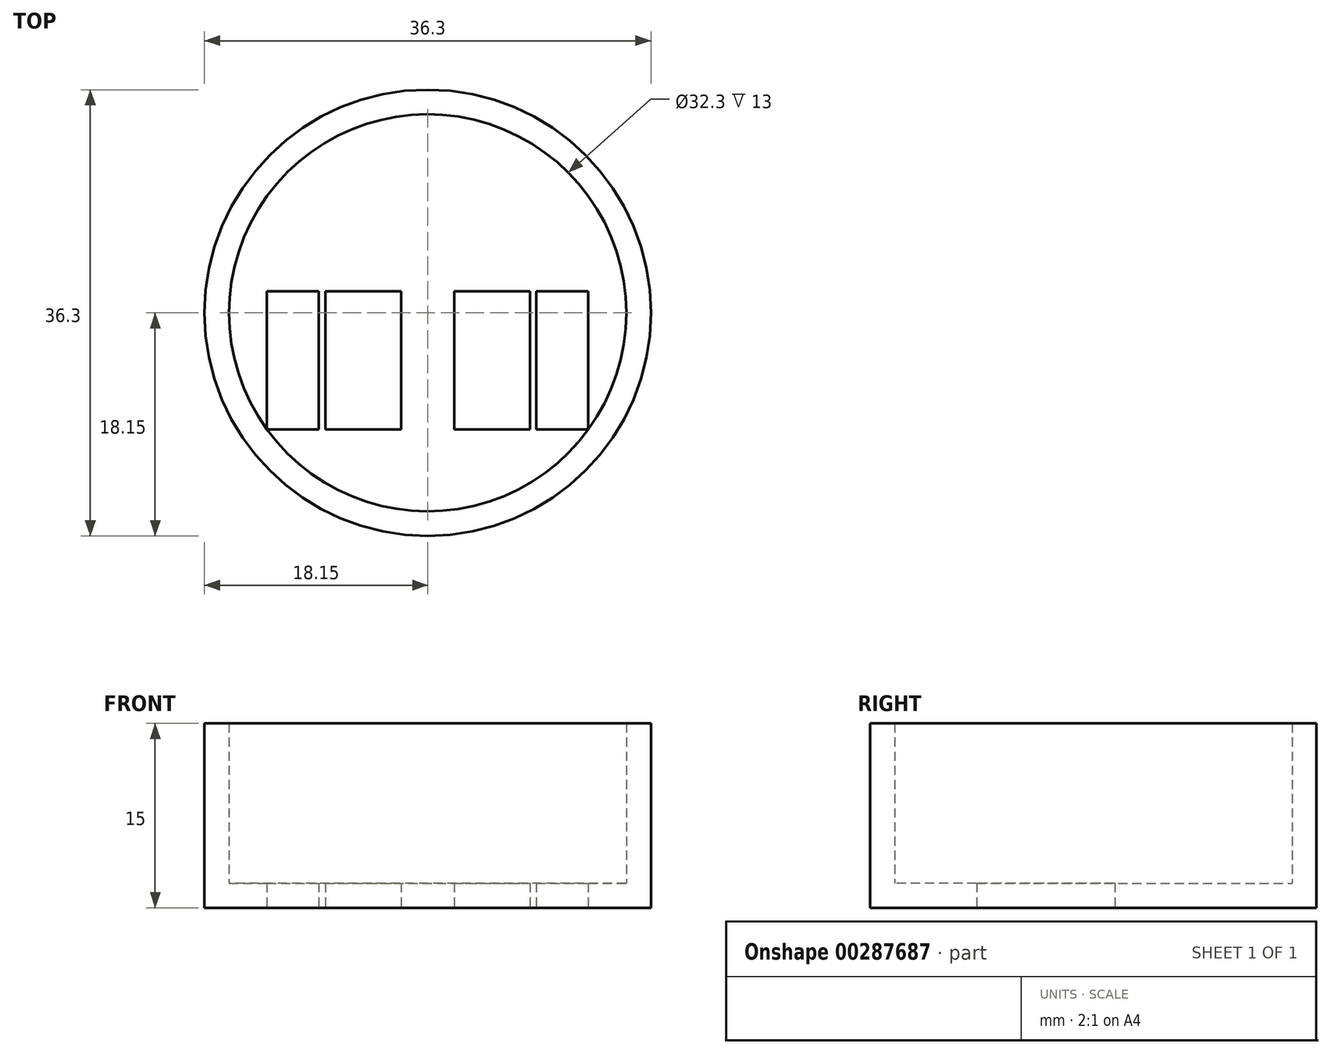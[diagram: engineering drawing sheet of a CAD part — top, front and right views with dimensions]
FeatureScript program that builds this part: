
annotation { "Feature Type Name" : "Feature", "Feature Type Description" : "" }
export const myFeature = defineFeature(function(context is Context, id is Id, definition is map)
    precondition{}
    {
        {
            var Q0;
            Q0=qCreatedBy(makeId("Top.planeOp"),FACE);
            var sketch = newSketch(context, id + "F0", { "sketchPlane" : qUnion([Q0])});
            skCircle(sketch, "E0", {"center": v(0, 0) * mm, "radius": 18.15 * mm});
            skLineSegment(sketch, "E1.bottom", {"start": v(-8.84, 15.85) * mm, "end": v(8.84, 15.85) * mm});
            skLineSegment(sketch, "E1.top", {"start": v(-8.84, -15.85) * mm, "end": v(8.84, -15.85) * mm});
            skLineSegment(sketch, "E1.left", {"start": v(-8.84, 15.85) * mm, "end": v(-8.84, -15.85) * mm});
            skLineSegment(sketch, "E1.right", {"start": v(8.84, 15.85) * mm, "end": v(8.84, -15.85) * mm});
            skLineSegment(sketch, "E2.bottom", {"start": v(-2.15, 18.02) * mm, "end": v(2.15, 18.02) * mm});
            skLineSegment(sketch, "E2.top", {"start": v(-2.15, -18.02) * mm, "end": v(2.15, -18.02) * mm});
            skLineSegment(sketch, "E2.left", {"start": v(-2.15, 18.02) * mm, "end": v(-2.15, -18.02) * mm});
            skLineSegment(sketch, "E2.right", {"start": v(2.15, 18.02) * mm, "end": v(2.15, -18.02) * mm});
            skLineSegment(sketch, "E3.bottom", {"start": v(-18.07, 1.75) * mm, "end": v(18.07, 1.75) * mm});
            skLineSegment(sketch, "E3.top", {"start": v(-18.07, -1.75) * mm, "end": v(18.07, -1.75) * mm});
            skLineSegment(sketch, "E3.left", {"start": v(-18.07, 1.75) * mm, "end": v(-18.07, -1.75) * mm});
            skLineSegment(sketch, "E3.right", {"start": v(18.07, 1.75) * mm, "end": v(18.07, -1.75) * mm});
            skLineSegment(sketch, "E4.bottom", {"start": v(-15.07, 1.75) * mm, "end": v(15.07, 1.75) * mm});
            skLineSegment(sketch, "E4.top", {"start": v(-15.07, -1.75) * mm, "end": v(15.07, -1.75) * mm});
            skLineSegment(sketch, "E4.left", {"start": v(-15.07, 1.75) * mm, "end": v(-15.07, -1.75) * mm});
            skLineSegment(sketch, "E4.right", {"start": v(15.07, 1.75) * mm, "end": v(15.07, -1.75) * mm});
            skCircle(sketch, "E5", {"center": v(0, 0) * mm, "radius": 16.15 * mm});
            skLineSegment(sketch, "E6.bottom", {"start": v(8.3, 13.85) * mm, "end": v(-8.3, 13.85) * mm});
            skLineSegment(sketch, "E6.top", {"start": v(8.3, -13.85) * mm, "end": v(-8.3, -13.85) * mm});
            skLineSegment(sketch, "E6.left", {"start": v(8.3, 13.85) * mm, "end": v(8.3, -13.85) * mm});
            skLineSegment(sketch, "E6.right", {"start": v(-8.3, 13.85) * mm, "end": v(-8.3, -13.85) * mm});
            skLineSegment(sketch, "E7.bottom", {"start": v(-13.07, 9.5) * mm, "end": v(13.07, 9.5) * mm});
            skLineSegment(sketch, "E7.top", {"start": v(-13.07, -9.5) * mm, "end": v(13.07, -9.5) * mm});
            skLineSegment(sketch, "E7.left", {"start": v(-13.07, 9.5) * mm, "end": v(-13.07, -9.5) * mm});
            skLineSegment(sketch, "E7.right", {"start": v(13.07, 9.5) * mm, "end": v(13.07, -9.5) * mm});
            skSolve(sketch);
        }
        {
            var Q0;
            Q0 = qSketchRegion(id + "F0", true);
            extrude(context, id + "F1", {"entities" : qUnion([Q0]), "depth" : 15 * mm});
        }
        {
            var Q0;
            {var subQ0=sQuery(id+"F0.wireOp",EDGE,"E2.bottom");Q0=makeQuery(id+"F0.imprint","IMPRINT",FACE,{"disambiguationData":[TD([[makeQuery(id+"F0.imprint","IMPRINT",EDGE,{"derivedFrom":subQ0}),1.0]])]});}
            var Q1;
            {var subQ0=sQuery(id+"F0.wireOp",EDGE,"E3.left");Q1=makeQuery(id+"F0.imprint","IMPRINT",FACE,{"disambiguationData":[TD([[makeQuery(id+"F0.imprint","IMPRINT",EDGE,{"derivedFrom":subQ0}),-1.0]])]});}
            var Q2;
            {var subQ0=sQuery(id+"F0.wireOp",EDGE,"E2.top");Q2=makeQuery(id+"F0.imprint","IMPRINT",FACE,{"disambiguationData":[TD([[makeQuery(id+"F0.imprint","IMPRINT",EDGE,{"derivedFrom":subQ0}),-1.0]])]});}
            var Q3;
            {var subQ0=sQuery(id+"F0.wireOp",EDGE,"E3.right");Q3=makeQuery(id+"F0.imprint","IMPRINT",FACE,{"disambiguationData":[TD([[makeQuery(id+"F0.imprint","IMPRINT",EDGE,{"derivedFrom":subQ0}),1.0]])]});}
            var Q4;
            {var subQ0=sQuery(id+"F0.wireOp",EDGE,"E1.bottom");var subQ5=sQuery(id+"F0.wireOp",EDGE,"E5");var subQ6=makeQuery(id+"F0.imprint","INTERSECT",VERTEX,{"disambiguationData":[OD(1.0)],"derivedFrom":[subQ0,subQ5]});Q4=makeQuery(id+"F0.imprint","IMPRINT",FACE,{"disambiguationData":[TD([[makeQuery(id+"F0.imprint","IMPRINT",EDGE,{"disambiguationData":[TD([[subQ6,-1.0]])],"derivedFrom":subQ5}),-1.0]])]});}
            var Q5;
            {var subQ0=sQuery(id+"F0.wireOp",EDGE,"E1.bottom");var subQ5=sQuery(id+"F0.wireOp",EDGE,"E5");var subQ7=makeQuery(id+"F0.imprint","INTERSECT",VERTEX,{"disambiguationData":[OD(0.0)],"derivedFrom":[subQ0,subQ5]});Q5=makeQuery(id+"F0.imprint","IMPRINT",FACE,{"disambiguationData":[TD([[makeQuery(id+"F0.imprint","IMPRINT",EDGE,{"disambiguationData":[TD([[subQ7,1.0]])],"derivedFrom":subQ5}),-1.0]])]});}
            var Q6;
            {var subQ0=sQuery(id+"F0.wireOp",EDGE,"E1.top");var subQ5=sQuery(id+"F0.wireOp",EDGE,"E5");var subQ6=makeQuery(id+"F0.imprint","INTERSECT",VERTEX,{"disambiguationData":[OD(0.0)],"derivedFrom":[subQ0,subQ5]});Q6=makeQuery(id+"F0.imprint","IMPRINT",FACE,{"disambiguationData":[TD([[makeQuery(id+"F0.imprint","IMPRINT",EDGE,{"disambiguationData":[TD([[subQ6,-1.0]])],"derivedFrom":subQ5}),-1.0]])]});}
            var Q7;
            {var subQ0=sQuery(id+"F0.wireOp",EDGE,"E1.top");var subQ5=sQuery(id+"F0.wireOp",EDGE,"E5");var subQ7=makeQuery(id+"F0.imprint","INTERSECT",VERTEX,{"disambiguationData":[OD(1.0)],"derivedFrom":[subQ0,subQ5]});Q7=makeQuery(id+"F0.imprint","IMPRINT",FACE,{"disambiguationData":[TD([[makeQuery(id+"F0.imprint","IMPRINT",EDGE,{"disambiguationData":[TD([[subQ7,1.0]])],"derivedFrom":subQ5}),-1.0]])]});}
            var Q8;
            {var subQ3=sQuery(id+"F0.wireOp",EDGE,"E5");var subQ5=sQuery(id+"F0.wireOp",EDGE,"E1.right");var subQ7=makeQuery(id+"F0.imprint","INTERSECT",VERTEX,{"disambiguationData":[OD(0.0)],"derivedFrom":[subQ5,subQ3]});Q8=makeQuery(id+"F0.imprint","IMPRINT",FACE,{"disambiguationData":[TD([[makeQuery(id+"F0.imprint","IMPRINT",EDGE,{"disambiguationData":[TD([[subQ7,1.0]])],"derivedFrom":subQ5}),1.0]])]});}
            var Q9;
            {var subQ3=sQuery(id+"F0.wireOp",EDGE,"E5");var subQ5=sQuery(id+"F0.wireOp",EDGE,"E1.left");var subQ7=makeQuery(id+"F0.imprint","INTERSECT",VERTEX,{"disambiguationData":[OD(0.0)],"derivedFrom":[subQ5,subQ3]});Q9=makeQuery(id+"F0.imprint","IMPRINT",FACE,{"disambiguationData":[TD([[makeQuery(id+"F0.imprint","IMPRINT",EDGE,{"disambiguationData":[TD([[subQ7,1.0]])],"derivedFrom":subQ5}),-1.0]])]});}
            var Q10;
            {var subQ0=sQuery(id+"F0.wireOp",EDGE,"E5");var subQ6=sQuery(id+"F0.wireOp",EDGE,"E1.left");var subQ8=makeQuery(id+"F0.imprint","INTERSECT",VERTEX,{"disambiguationData":[OD(1.0)],"derivedFrom":[subQ6,subQ0]});Q10=makeQuery(id+"F0.imprint","IMPRINT",FACE,{"disambiguationData":[TD([[makeQuery(id+"F0.imprint","IMPRINT",EDGE,{"disambiguationData":[TD([[subQ8,-1.0]])],"derivedFrom":subQ6}),-1.0]])]});}
            var Q11;
            {var subQ0=sQuery(id+"F0.wireOp",EDGE,"E5");var subQ2=sQuery(id+"F0.wireOp",EDGE,"E1.right");var subQ3=makeQuery(id+"F0.imprint","INTERSECT",VERTEX,{"disambiguationData":[OD(1.0)],"derivedFrom":[subQ2,subQ0]});Q11=makeQuery(id+"F0.imprint","IMPRINT",FACE,{"disambiguationData":[TD([[makeQuery(id+"F0.imprint","IMPRINT",EDGE,{"disambiguationData":[TD([[subQ3,-1.0]])],"derivedFrom":subQ2}),1.0]])]});}
            var Q12;
            {var subQ1=sQuery(id+"F0.wireOp",EDGE,"E1.bottom");var subQ3=sQuery(id+"F0.wireOp",EDGE,"E5");var subQ4=makeQuery(id+"F0.imprint","INTERSECT",VERTEX,{"disambiguationData":[OD(0.0)],"derivedFrom":[subQ1,subQ3]});Q12=makeQuery(id+"F0.imprint","IMPRINT",FACE,{"disambiguationData":[TD([[makeQuery(id+"F0.imprint","IMPRINT",EDGE,{"disambiguationData":[TD([[subQ4,1.0]])],"derivedFrom":subQ1}),-1.0]])]});}
            var Q13;
            {var subQ1=sQuery(id+"F0.wireOp",EDGE,"E1.bottom");var subQ3=sQuery(id+"F0.wireOp",EDGE,"E5");var subQ4=makeQuery(id+"F0.imprint","INTERSECT",VERTEX,{"disambiguationData":[OD(1.0)],"derivedFrom":[subQ1,subQ3]});Q13=makeQuery(id+"F0.imprint","IMPRINT",FACE,{"disambiguationData":[TD([[makeQuery(id+"F0.imprint","IMPRINT",EDGE,{"disambiguationData":[TD([[subQ4,-1.0]])],"derivedFrom":subQ1}),-1.0]])]});}
            var Q14;
            {var subQ1=sQuery(id+"F0.wireOp",EDGE,"E1.top");var subQ3=sQuery(id+"F0.wireOp",EDGE,"E5");var subQ4=makeQuery(id+"F0.imprint","INTERSECT",VERTEX,{"disambiguationData":[OD(0.0)],"derivedFrom":[subQ1,subQ3]});Q14=makeQuery(id+"F0.imprint","IMPRINT",FACE,{"disambiguationData":[TD([[makeQuery(id+"F0.imprint","IMPRINT",EDGE,{"disambiguationData":[TD([[subQ4,1.0]])],"derivedFrom":subQ1}),1.0]])]});}
            var Q15;
            {var subQ1=sQuery(id+"F0.wireOp",EDGE,"E1.top");var subQ3=sQuery(id+"F0.wireOp",EDGE,"E5");var subQ4=makeQuery(id+"F0.imprint","INTERSECT",VERTEX,{"disambiguationData":[OD(1.0)],"derivedFrom":[subQ1,subQ3]});Q15=makeQuery(id+"F0.imprint","IMPRINT",FACE,{"disambiguationData":[TD([[makeQuery(id+"F0.imprint","IMPRINT",EDGE,{"disambiguationData":[TD([[subQ4,-1.0]])],"derivedFrom":subQ1}),1.0]])]});}
            var Q16;
            {var subQ0=sQuery(id+"F0.wireOp",EDGE,"E2.bottom");Q16=makeQuery(id+"F0.imprint","IMPRINT",FACE,{"disambiguationData":[TD([[makeQuery(id+"F0.imprint","IMPRINT",EDGE,{"derivedFrom":subQ0}),-1.0]])]});}
            var Q17;
            {var subQ0=sQuery(id+"F0.wireOp",EDGE,"E2.top");Q17=makeQuery(id+"F0.imprint","IMPRINT",FACE,{"disambiguationData":[TD([[makeQuery(id+"F0.imprint","IMPRINT",EDGE,{"derivedFrom":subQ0}),1.0]])]});}
            var Q18;
            {var subQ0=sQuery(id+"F0.wireOp",EDGE,"E3.left");Q18=makeQuery(id+"F0.imprint","IMPRINT",FACE,{"disambiguationData":[TD([[makeQuery(id+"F0.imprint","IMPRINT",EDGE,{"derivedFrom":subQ0}),1.0]])]});}
            var Q19;
            {var subQ0=sQuery(id+"F0.wireOp",EDGE,"E3.right");Q19=makeQuery(id+"F0.imprint","IMPRINT",FACE,{"disambiguationData":[TD([[makeQuery(id+"F0.imprint","IMPRINT",EDGE,{"derivedFrom":subQ0}),-1.0]])]});}
            var Q20;
            {var subQ0=sQuery(id+"F0.wireOp",EDGE,"E6.bottom");var subQ1=sQuery(id+"F0.wireOp",EDGE,"E2.left");var subQ2=makeQuery(id+"F0.imprint","INTERSECT",VERTEX,{"derivedFrom":[subQ1,subQ0]});Q20=makeQuery(id+"F0.imprint","IMPRINT",FACE,{"disambiguationData":[TD([[makeQuery(id+"F0.imprint","IMPRINT",EDGE,{"disambiguationData":[TD([[subQ2,-1.0]])],"derivedFrom":subQ1}),1.0]])]});}
            var Q21;
            {var subQ0=sQuery(id+"F0.wireOp",EDGE,"E4.bottom");var subQ1=sQuery(id+"F0.wireOp",EDGE,"E1.right");var subQ2=makeQuery(id+"F0.imprint","INTERSECT",VERTEX,{"derivedFrom":[subQ1,subQ0]});Q21=makeQuery(id+"F0.imprint","IMPRINT",FACE,{"disambiguationData":[TD([[makeQuery(id+"F0.imprint","IMPRINT",EDGE,{"disambiguationData":[TD([[subQ2,-1.0]])],"derivedFrom":subQ1}),1.0]])]});}
            var Q22;
            {var subQ0=sQuery(id+"F0.wireOp",EDGE,"E7.bottom");var subQ1=sQuery(id+"F0.wireOp",EDGE,"E1.left");var subQ2=makeQuery(id+"F0.imprint","INTERSECT",VERTEX,{"derivedFrom":[subQ1,subQ0]});Q22=makeQuery(id+"F0.imprint","IMPRINT",FACE,{"disambiguationData":[TD([[makeQuery(id+"F0.imprint","IMPRINT",EDGE,{"disambiguationData":[TD([[subQ2,-1.0]])],"derivedFrom":subQ1}),-1.0]])]});}
            var Q23;
            {var subQ0=sQuery(id+"F0.wireOp",EDGE,"E2.right");var subQ1=sQuery(id+"F0.wireOp",EDGE,"E1.top");var subQ2=makeQuery(id+"F0.imprint","INTERSECT",VERTEX,{"derivedFrom":[subQ1,subQ0]});Q23=makeQuery(id+"F0.imprint","IMPRINT",FACE,{"disambiguationData":[TD([[makeQuery(id+"F0.imprint","IMPRINT",EDGE,{"disambiguationData":[TD([[subQ2,-1.0]])],"derivedFrom":subQ1}),1.0]])]});}
            var Q24;
            {var subQ0=sQuery(id+"F0.wireOp",EDGE,"E4.top");var subQ1=sQuery(id+"F0.wireOp",EDGE,"E1.left");var subQ2=makeQuery(id+"F0.imprint","INTERSECT",VERTEX,{"derivedFrom":[subQ1,subQ0]});Q24=makeQuery(id+"F0.imprint","IMPRINT",FACE,{"disambiguationData":[TD([[makeQuery(id+"F0.imprint","IMPRINT",EDGE,{"disambiguationData":[TD([[subQ2,-1.0]])],"derivedFrom":subQ1}),-1.0]])]});}
            var Q25;
            {var subQ0=sQuery(id+"F0.wireOp",EDGE,"E5");var subQ1=sQuery(id+"F0.wireOp",EDGE,"E1.right");var subQ2=makeQuery(id+"F0.imprint","INTERSECT",VERTEX,{"disambiguationData":[OD(0.0)],"derivedFrom":[subQ1,subQ0]});Q25=makeQuery(id+"F0.imprint","IMPRINT",FACE,{"disambiguationData":[TD([[makeQuery(id+"F0.imprint","IMPRINT",EDGE,{"disambiguationData":[TD([[subQ2,-1.0]])],"derivedFrom":subQ1}),1.0]])]});}
            var Q26;
            {var subQ0=sQuery(id+"F0.wireOp",EDGE,"E7.top");var subQ1=sQuery(id+"F0.wireOp",EDGE,"E1.left");var subQ2=makeQuery(id+"F0.imprint","INTERSECT",VERTEX,{"derivedFrom":[subQ1,subQ0]});Q26=makeQuery(id+"F0.imprint","IMPRINT",FACE,{"disambiguationData":[TD([[makeQuery(id+"F0.imprint","IMPRINT",EDGE,{"disambiguationData":[TD([[subQ2,-1.0]])],"derivedFrom":subQ1}),-1.0]])]});}
            var Q27;
            {var subQ0=sQuery(id+"F0.wireOp",EDGE,"E7.top");var subQ1=sQuery(id+"F0.wireOp",EDGE,"E1.right");var subQ2=makeQuery(id+"F0.imprint","INTERSECT",VERTEX,{"derivedFrom":[subQ1,subQ0]});Q27=makeQuery(id+"F0.imprint","IMPRINT",FACE,{"disambiguationData":[TD([[makeQuery(id+"F0.imprint","IMPRINT",EDGE,{"disambiguationData":[TD([[subQ2,-1.0]])],"derivedFrom":subQ1}),1.0]])]});}
            var Q28;
            {var subQ0=sQuery(id+"F0.wireOp",EDGE,"E7.bottom");var subQ1=sQuery(id+"F0.wireOp",EDGE,"E1.right");var subQ2=makeQuery(id+"F0.imprint","INTERSECT",VERTEX,{"derivedFrom":[subQ1,subQ0]});Q28=makeQuery(id+"F0.imprint","IMPRINT",FACE,{"disambiguationData":[TD([[makeQuery(id+"F0.imprint","IMPRINT",EDGE,{"disambiguationData":[TD([[subQ2,-1.0]])],"derivedFrom":subQ1}),1.0]])]});}
            var Q29;
            {var subQ1=sQuery(id+"F0.wireOp",EDGE,"E3.bottom");var subQ3=sQuery(id+"F0.wireOp",EDGE,"E5");var subQ4=makeQuery(id+"F0.imprint","INTERSECT",VERTEX,{"disambiguationData":[OD(0.0)],"derivedFrom":[subQ1,subQ3]});Q29=makeQuery(id+"F0.imprint","IMPRINT",FACE,{"disambiguationData":[TD([[makeQuery(id+"F0.imprint","IMPRINT",EDGE,{"disambiguationData":[TD([[subQ4,-1.0]])],"derivedFrom":subQ1}),1.0]])]});}
            var Q30;
            {var subQ1=sQuery(id+"F0.wireOp",EDGE,"E3.top");var subQ3=sQuery(id+"F0.wireOp",EDGE,"E5");var subQ4=makeQuery(id+"F0.imprint","INTERSECT",VERTEX,{"disambiguationData":[OD(1.0)],"derivedFrom":[subQ1,subQ3]});Q30=makeQuery(id+"F0.imprint","IMPRINT",FACE,{"disambiguationData":[TD([[makeQuery(id+"F0.imprint","IMPRINT",EDGE,{"disambiguationData":[TD([[subQ4,1.0]])],"derivedFrom":subQ1}),-1.0]])]});}
            var Q31;
            {var subQ0=sQuery(id+"F0.wireOp",EDGE,"E4.top");var subQ1=sQuery(id+"F0.wireOp",EDGE,"E2.left");var subQ2=makeQuery(id+"F0.imprint","INTERSECT",VERTEX,{"derivedFrom":[subQ1,subQ0]});Q31=makeQuery(id+"F0.imprint","IMPRINT",FACE,{"disambiguationData":[TD([[makeQuery(id+"F0.imprint","IMPRINT",EDGE,{"disambiguationData":[TD([[subQ2,-1.0]])],"derivedFrom":subQ1}),1.0]])]});}
            var Q32;
            {var subQ0=sQuery(id+"F0.wireOp",EDGE,"E6.bottom");var subQ1=sQuery(id+"F0.wireOp",EDGE,"E2.right");var subQ2=makeQuery(id+"F0.imprint","INTERSECT",VERTEX,{"derivedFrom":[subQ1,subQ0]});Q32=makeQuery(id+"F0.imprint","IMPRINT",FACE,{"disambiguationData":[TD([[makeQuery(id+"F0.imprint","IMPRINT",EDGE,{"disambiguationData":[TD([[subQ2,-1.0]])],"derivedFrom":subQ1}),1.0]])]});}
            var Q33;
            {var subQ0=sQuery(id+"F0.wireOp",EDGE,"E7.bottom");var subQ1=sQuery(id+"F0.wireOp",EDGE,"E2.left");var subQ2=makeQuery(id+"F0.imprint","INTERSECT",VERTEX,{"derivedFrom":[subQ1,subQ0]});Q33=makeQuery(id+"F0.imprint","IMPRINT",FACE,{"disambiguationData":[TD([[makeQuery(id+"F0.imprint","IMPRINT",EDGE,{"disambiguationData":[TD([[subQ2,-1.0]])],"derivedFrom":subQ1}),-1.0]])]});}
            var Q34;
            {var subQ0=sQuery(id+"F0.wireOp",EDGE,"E4.top");var subQ1=sQuery(id+"F0.wireOp",EDGE,"E1.right");var subQ2=makeQuery(id+"F0.imprint","INTERSECT",VERTEX,{"derivedFrom":[subQ1,subQ0]});Q34=makeQuery(id+"F0.imprint","IMPRINT",FACE,{"disambiguationData":[TD([[makeQuery(id+"F0.imprint","IMPRINT",EDGE,{"disambiguationData":[TD([[subQ2,-1.0]])],"derivedFrom":subQ1}),1.0]])]});}
            var Q35;
            {var subQ0=sQuery(id+"F0.wireOp",EDGE,"E4.bottom");var subQ1=sQuery(id+"F0.wireOp",EDGE,"E2.right");var subQ2=makeQuery(id+"F0.imprint","INTERSECT",VERTEX,{"derivedFrom":[subQ1,subQ0]});Q35=makeQuery(id+"F0.imprint","IMPRINT",FACE,{"disambiguationData":[TD([[makeQuery(id+"F0.imprint","IMPRINT",EDGE,{"disambiguationData":[TD([[subQ2,-1.0]])],"derivedFrom":subQ1}),1.0]])]});}
            var Q36;
            {var subQ1=sQuery(id+"F0.wireOp",EDGE,"E3.bottom");var subQ3=sQuery(id+"F0.wireOp",EDGE,"E5");var subQ4=makeQuery(id+"F0.imprint","INTERSECT",VERTEX,{"disambiguationData":[OD(1.0)],"derivedFrom":[subQ1,subQ3]});Q36=makeQuery(id+"F0.imprint","IMPRINT",FACE,{"disambiguationData":[TD([[makeQuery(id+"F0.imprint","IMPRINT",EDGE,{"disambiguationData":[TD([[subQ4,1.0]])],"derivedFrom":subQ1}),1.0]])]});}
            var Q37;
            {var subQ0=sQuery(id+"F0.wireOp",EDGE,"E5");var subQ1=sQuery(id+"F0.wireOp",EDGE,"E1.bottom");var subQ2=makeQuery(id+"F0.imprint","INTERSECT",VERTEX,{"disambiguationData":[OD(0.0)],"derivedFrom":[subQ1,subQ0]});Q37=makeQuery(id+"F0.imprint","IMPRINT",FACE,{"disambiguationData":[TD([[makeQuery(id+"F0.imprint","IMPRINT",EDGE,{"disambiguationData":[TD([[subQ2,-1.0]])],"derivedFrom":subQ1}),-1.0]])]});}
            var Q38;
            {var subQ1=sQuery(id+"F0.wireOp",EDGE,"E3.top");var subQ3=sQuery(id+"F0.wireOp",EDGE,"E5");var subQ4=makeQuery(id+"F0.imprint","INTERSECT",VERTEX,{"disambiguationData":[OD(0.0)],"derivedFrom":[subQ1,subQ3]});Q38=makeQuery(id+"F0.imprint","IMPRINT",FACE,{"disambiguationData":[TD([[makeQuery(id+"F0.imprint","IMPRINT",EDGE,{"disambiguationData":[TD([[subQ4,-1.0]])],"derivedFrom":subQ1}),-1.0]])]});}
            var Q39;
            {var subQ0=sQuery(id+"F0.wireOp",EDGE,"E2.left");var subQ1=sQuery(id+"F0.wireOp",EDGE,"E1.bottom");var subQ2=makeQuery(id+"F0.imprint","INTERSECT",VERTEX,{"derivedFrom":[subQ1,subQ0]});Q39=makeQuery(id+"F0.imprint","IMPRINT",FACE,{"disambiguationData":[TD([[makeQuery(id+"F0.imprint","IMPRINT",EDGE,{"disambiguationData":[TD([[subQ2,-1.0]])],"derivedFrom":subQ1}),-1.0]])]});}
            var Q40;
            {var subQ0=sQuery(id+"F0.wireOp",EDGE,"E4.bottom");var subQ1=sQuery(id+"F0.wireOp",EDGE,"E2.left");var subQ2=makeQuery(id+"F0.imprint","INTERSECT",VERTEX,{"derivedFrom":[subQ1,subQ0]});Q40=makeQuery(id+"F0.imprint","IMPRINT",FACE,{"disambiguationData":[TD([[makeQuery(id+"F0.imprint","IMPRINT",EDGE,{"disambiguationData":[TD([[subQ2,-1.0]])],"derivedFrom":subQ1}),-1.0]])]});}
            var Q41;
            {var subQ0=sQuery(id+"F0.wireOp",EDGE,"E7.top");var subQ1=sQuery(id+"F0.wireOp",EDGE,"E2.left");var subQ2=makeQuery(id+"F0.imprint","INTERSECT",VERTEX,{"derivedFrom":[subQ1,subQ0]});Q41=makeQuery(id+"F0.imprint","IMPRINT",FACE,{"disambiguationData":[TD([[makeQuery(id+"F0.imprint","IMPRINT",EDGE,{"disambiguationData":[TD([[subQ2,-1.0]])],"derivedFrom":subQ1}),-1.0]])]});}
            var Q42;
            {var subQ0=sQuery(id+"F0.wireOp",EDGE,"E5");var subQ1=sQuery(id+"F0.wireOp",EDGE,"E1.left");var subQ2=makeQuery(id+"F0.imprint","INTERSECT",VERTEX,{"disambiguationData":[OD(0.0)],"derivedFrom":[subQ1,subQ0]});Q42=makeQuery(id+"F0.imprint","IMPRINT",FACE,{"disambiguationData":[TD([[makeQuery(id+"F0.imprint","IMPRINT",EDGE,{"disambiguationData":[TD([[subQ2,-1.0]])],"derivedFrom":subQ1}),-1.0]])]});}
            var Q43;
            {var subQ0=sQuery(id+"F0.wireOp",EDGE,"E7.top");var subQ1=sQuery(id+"F0.wireOp",EDGE,"E2.right");var subQ2=makeQuery(id+"F0.imprint","INTERSECT",VERTEX,{"derivedFrom":[subQ1,subQ0]});Q43=makeQuery(id+"F0.imprint","IMPRINT",FACE,{"disambiguationData":[TD([[makeQuery(id+"F0.imprint","IMPRINT",EDGE,{"disambiguationData":[TD([[subQ2,-1.0]])],"derivedFrom":subQ1}),1.0]])]});}
            var Q44;
            {var subQ0=sQuery(id+"F0.wireOp",EDGE,"E7.bottom");var subQ1=sQuery(id+"F0.wireOp",EDGE,"E2.left");var subQ2=makeQuery(id+"F0.imprint","INTERSECT",VERTEX,{"derivedFrom":[subQ1,subQ0]});Q44=makeQuery(id+"F0.imprint","IMPRINT",FACE,{"disambiguationData":[TD([[makeQuery(id+"F0.imprint","IMPRINT",EDGE,{"disambiguationData":[TD([[subQ2,-1.0]])],"derivedFrom":subQ1}),1.0]])]});}
            var Q45;
            {var subQ0=sQuery(id+"F0.wireOp",EDGE,"E7.bottom");var subQ1=sQuery(id+"F0.wireOp",EDGE,"E2.right");var subQ2=makeQuery(id+"F0.imprint","INTERSECT",VERTEX,{"derivedFrom":[subQ1,subQ0]});Q45=makeQuery(id+"F0.imprint","IMPRINT",FACE,{"disambiguationData":[TD([[makeQuery(id+"F0.imprint","IMPRINT",EDGE,{"disambiguationData":[TD([[subQ2,-1.0]])],"derivedFrom":subQ1}),1.0]])]});}
            var Q46;
            {var subQ0=sQuery(id+"F0.wireOp",EDGE,"E7.top");var subQ1=sQuery(id+"F0.wireOp",EDGE,"E2.left");var subQ2=makeQuery(id+"F0.imprint","INTERSECT",VERTEX,{"derivedFrom":[subQ1,subQ0]});Q46=makeQuery(id+"F0.imprint","IMPRINT",FACE,{"disambiguationData":[TD([[makeQuery(id+"F0.imprint","IMPRINT",EDGE,{"disambiguationData":[TD([[subQ2,-1.0]])],"derivedFrom":subQ1}),1.0]])]});}
            var Q47;
            {var subQ0=sQuery(id+"F0.wireOp",EDGE,"E4.bottom");var subQ1=sQuery(id+"F0.wireOp",EDGE,"E1.left");var subQ2=makeQuery(id+"F0.imprint","INTERSECT",VERTEX,{"derivedFrom":[subQ1,subQ0]});Q47=makeQuery(id+"F0.imprint","IMPRINT",FACE,{"disambiguationData":[TD([[makeQuery(id+"F0.imprint","IMPRINT",EDGE,{"disambiguationData":[TD([[subQ2,-1.0]])],"derivedFrom":subQ1}),-1.0]])]});}
            var Q48;
            {var subQ0=sQuery(id+"F0.wireOp",EDGE,"E6.bottom");var subQ1=sQuery(id+"F0.wireOp",EDGE,"E2.left");var subQ2=makeQuery(id+"F0.imprint","INTERSECT",VERTEX,{"derivedFrom":[subQ1,subQ0]});Q48=makeQuery(id+"F0.imprint","IMPRINT",FACE,{"disambiguationData":[TD([[makeQuery(id+"F0.imprint","IMPRINT",EDGE,{"disambiguationData":[TD([[subQ2,-1.0]])],"derivedFrom":subQ1}),-1.0]])]});}
            var Q49;
            {var subQ0=sQuery(id+"F0.wireOp",EDGE,"E4.top");var subQ1=sQuery(id+"F0.wireOp",EDGE,"E2.left");var subQ2=makeQuery(id+"F0.imprint","INTERSECT",VERTEX,{"derivedFrom":[subQ1,subQ0]});Q49=makeQuery(id+"F0.imprint","IMPRINT",FACE,{"disambiguationData":[TD([[makeQuery(id+"F0.imprint","IMPRINT",EDGE,{"disambiguationData":[TD([[subQ2,-1.0]])],"derivedFrom":subQ1}),-1.0]])]});}
            var Q50;
            {var subQ0=sQuery(id+"F0.wireOp",EDGE,"E4.top");var subQ1=sQuery(id+"F0.wireOp",EDGE,"E2.right");var subQ2=makeQuery(id+"F0.imprint","INTERSECT",VERTEX,{"derivedFrom":[subQ1,subQ0]});Q50=makeQuery(id+"F0.imprint","IMPRINT",FACE,{"disambiguationData":[TD([[makeQuery(id+"F0.imprint","IMPRINT",EDGE,{"disambiguationData":[TD([[subQ2,-1.0]])],"derivedFrom":subQ1}),1.0]])]});}
            var Q51;
            {var subQ0=sQuery(id+"F0.wireOp",EDGE,"E7.bottom");var subQ1=sQuery(id+"F0.wireOp",EDGE,"E1.left");var subQ2=makeQuery(id+"F0.imprint","INTERSECT",VERTEX,{"derivedFrom":[subQ1,subQ0]});Q51=makeQuery(id+"F0.imprint","IMPRINT",FACE,{"disambiguationData":[TD([[makeQuery(id+"F0.imprint","IMPRINT",EDGE,{"disambiguationData":[TD([[subQ2,-1.0]])],"derivedFrom":subQ1}),1.0]])]});}
            var Q52;
            {var subQ0=sQuery(id+"F0.wireOp",EDGE,"E4.bottom");var subQ1=sQuery(id+"F0.wireOp",EDGE,"E1.left");var subQ2=makeQuery(id+"F0.imprint","INTERSECT",VERTEX,{"derivedFrom":[subQ1,subQ0]});Q52=makeQuery(id+"F0.imprint","IMPRINT",FACE,{"disambiguationData":[TD([[makeQuery(id+"F0.imprint","IMPRINT",EDGE,{"disambiguationData":[TD([[subQ2,-1.0]])],"derivedFrom":subQ1}),1.0]])]});}
            var Q53;
            {var subQ0=sQuery(id+"F0.wireOp",EDGE,"E2.left");var subQ1=sQuery(id+"F0.wireOp",EDGE,"E1.bottom");var subQ2=makeQuery(id+"F0.imprint","INTERSECT",VERTEX,{"derivedFrom":[subQ1,subQ0]});Q53=makeQuery(id+"F0.imprint","IMPRINT",FACE,{"disambiguationData":[TD([[makeQuery(id+"F0.imprint","IMPRINT",EDGE,{"disambiguationData":[TD([[subQ2,-1.0]])],"derivedFrom":subQ1}),1.0]])]});}
            var Q54;
            {var subQ0=sQuery(id+"F0.wireOp",EDGE,"E2.right");var subQ1=sQuery(id+"F0.wireOp",EDGE,"E1.bottom");var subQ2=makeQuery(id+"F0.imprint","INTERSECT",VERTEX,{"derivedFrom":[subQ1,subQ0]});Q54=makeQuery(id+"F0.imprint","IMPRINT",FACE,{"disambiguationData":[TD([[makeQuery(id+"F0.imprint","IMPRINT",EDGE,{"disambiguationData":[TD([[subQ2,-1.0]])],"derivedFrom":subQ1}),-1.0]])]});}
            var Q55;
            {var subQ0=sQuery(id+"F0.wireOp",EDGE,"E5");var subQ1=sQuery(id+"F0.wireOp",EDGE,"E1.right");var subQ2=makeQuery(id+"F0.imprint","INTERSECT",VERTEX,{"disambiguationData":[OD(0.0)],"derivedFrom":[subQ1,subQ0]});Q55=makeQuery(id+"F0.imprint","IMPRINT",FACE,{"disambiguationData":[TD([[makeQuery(id+"F0.imprint","IMPRINT",EDGE,{"disambiguationData":[TD([[subQ2,-1.0]])],"derivedFrom":subQ1}),-1.0]])]});}
            var Q56;
            {var subQ0=sQuery(id+"F0.wireOp",EDGE,"E2.left");var subQ1=sQuery(id+"F0.wireOp",EDGE,"E1.top");var subQ2=makeQuery(id+"F0.imprint","INTERSECT",VERTEX,{"derivedFrom":[subQ1,subQ0]});Q56=makeQuery(id+"F0.imprint","IMPRINT",FACE,{"disambiguationData":[TD([[makeQuery(id+"F0.imprint","IMPRINT",EDGE,{"disambiguationData":[TD([[subQ2,-1.0]])],"derivedFrom":subQ1}),1.0]])]});}
            var Q57;
            {var subQ0=sQuery(id+"F0.wireOp",EDGE,"E7.top");var subQ1=sQuery(id+"F0.wireOp",EDGE,"E1.left");var subQ2=makeQuery(id+"F0.imprint","INTERSECT",VERTEX,{"derivedFrom":[subQ1,subQ0]});Q57=makeQuery(id+"F0.imprint","IMPRINT",FACE,{"disambiguationData":[TD([[makeQuery(id+"F0.imprint","IMPRINT",EDGE,{"disambiguationData":[TD([[subQ2,-1.0]])],"derivedFrom":subQ1}),1.0]])]});}
            var Q58;
            {var subQ0=sQuery(id+"F0.wireOp",EDGE,"E5");var subQ1=sQuery(id+"F0.wireOp",EDGE,"E1.top");var subQ2=makeQuery(id+"F0.imprint","INTERSECT",VERTEX,{"disambiguationData":[OD(0.0)],"derivedFrom":[subQ1,subQ0]});Q58=makeQuery(id+"F0.imprint","IMPRINT",FACE,{"disambiguationData":[TD([[makeQuery(id+"F0.imprint","IMPRINT",EDGE,{"disambiguationData":[TD([[subQ2,-1.0]])],"derivedFrom":subQ1}),1.0]])]});}
            var Q59;
            {var subQ0=sQuery(id+"F0.wireOp",EDGE,"E4.bottom");var subQ1=sQuery(id+"F0.wireOp",EDGE,"E1.right");var subQ2=makeQuery(id+"F0.imprint","INTERSECT",VERTEX,{"derivedFrom":[subQ1,subQ0]});Q59=makeQuery(id+"F0.imprint","IMPRINT",FACE,{"disambiguationData":[TD([[makeQuery(id+"F0.imprint","IMPRINT",EDGE,{"disambiguationData":[TD([[subQ2,-1.0]])],"derivedFrom":subQ1}),-1.0]])]});}
            var Q60;
            {var subQ0=sQuery(id+"F0.wireOp",EDGE,"E5");var subQ1=sQuery(id+"F0.wireOp",EDGE,"E1.left");var subQ2=makeQuery(id+"F0.imprint","INTERSECT",VERTEX,{"disambiguationData":[OD(0.0)],"derivedFrom":[subQ1,subQ0]});Q60=makeQuery(id+"F0.imprint","IMPRINT",FACE,{"disambiguationData":[TD([[makeQuery(id+"F0.imprint","IMPRINT",EDGE,{"disambiguationData":[TD([[subQ2,-1.0]])],"derivedFrom":subQ1}),1.0]])]});}
            var Q61;
            {var subQ0=sQuery(id+"F0.wireOp",EDGE,"E4.top");var subQ1=sQuery(id+"F0.wireOp",EDGE,"E1.right");var subQ2=makeQuery(id+"F0.imprint","INTERSECT",VERTEX,{"derivedFrom":[subQ1,subQ0]});Q61=makeQuery(id+"F0.imprint","IMPRINT",FACE,{"disambiguationData":[TD([[makeQuery(id+"F0.imprint","IMPRINT",EDGE,{"disambiguationData":[TD([[subQ2,-1.0]])],"derivedFrom":subQ1}),-1.0]])]});}
            var Q62;
            {var subQ0=sQuery(id+"F0.wireOp",EDGE,"E4.top");var subQ1=sQuery(id+"F0.wireOp",EDGE,"E1.left");var subQ2=makeQuery(id+"F0.imprint","INTERSECT",VERTEX,{"derivedFrom":[subQ1,subQ0]});Q62=makeQuery(id+"F0.imprint","IMPRINT",FACE,{"disambiguationData":[TD([[makeQuery(id+"F0.imprint","IMPRINT",EDGE,{"disambiguationData":[TD([[subQ2,-1.0]])],"derivedFrom":subQ1}),1.0]])]});}
            var Q63;
            {var subQ0=sQuery(id+"F0.wireOp",EDGE,"E7.bottom");var subQ1=sQuery(id+"F0.wireOp",EDGE,"E1.right");var subQ2=makeQuery(id+"F0.imprint","INTERSECT",VERTEX,{"derivedFrom":[subQ1,subQ0]});Q63=makeQuery(id+"F0.imprint","IMPRINT",FACE,{"disambiguationData":[TD([[makeQuery(id+"F0.imprint","IMPRINT",EDGE,{"disambiguationData":[TD([[subQ2,-1.0]])],"derivedFrom":subQ1}),-1.0]])]});}
            var Q64;
            {var subQ0=sQuery(id+"F0.wireOp",EDGE,"E7.top");var subQ1=sQuery(id+"F0.wireOp",EDGE,"E1.right");var subQ2=makeQuery(id+"F0.imprint","INTERSECT",VERTEX,{"derivedFrom":[subQ1,subQ0]});Q64=makeQuery(id+"F0.imprint","IMPRINT",FACE,{"disambiguationData":[TD([[makeQuery(id+"F0.imprint","IMPRINT",EDGE,{"disambiguationData":[TD([[subQ2,-1.0]])],"derivedFrom":subQ1}),-1.0]])]});}
            var Q65;
            Q65=makeQuery(id+"F1.opExtrude","CAP_FACE",FACE,{"disambiguationData":[OSD([sQuery(id+"F0.wireOp",EDGE,"E0"),sQuery(id+"F0.wireOp",EDGE,"E5")])],"isStart":true});
            var Q66;
            {var subQ0=sQuery(id+"F0.wireOp",EDGE,"E4.left");Q66=makeQuery(id+"F0.imprint","IMPRINT",FACE,{"disambiguationData":[TD([[makeQuery(id+"F0.imprint","IMPRINT",EDGE,{"derivedFrom":subQ0}),-1.0]])]});}
            var Q67;
            {var subQ0=sQuery(id+"F0.wireOp",EDGE,"E2.left");var subQ1=sQuery(id+"F0.wireOp",EDGE,"E1.top");var subQ2=makeQuery(id+"F0.imprint","INTERSECT",VERTEX,{"derivedFrom":[subQ1,subQ0]});Q67=makeQuery(id+"F0.imprint","IMPRINT",FACE,{"disambiguationData":[TD([[makeQuery(id+"F0.imprint","IMPRINT",EDGE,{"disambiguationData":[TD([[subQ2,-1.0]])],"derivedFrom":subQ1}),-1.0]])]});}
            var Q68;
            {var subQ0=sQuery(id+"F0.wireOp",EDGE,"E4.right");Q68=makeQuery(id+"F0.imprint","IMPRINT",FACE,{"disambiguationData":[TD([[makeQuery(id+"F0.imprint","IMPRINT",EDGE,{"derivedFrom":subQ0}),1.0]])]});}
            var Q69;
            {var subQ0=sQuery(id+"F0.wireOp",EDGE,"E4.right");Q69=makeQuery(id+"F0.imprint","IMPRINT",FACE,{"disambiguationData":[TD([[makeQuery(id+"F0.imprint","IMPRINT",EDGE,{"derivedFrom":subQ0}),-1.0]])]});}
            var Q70;
            {var subQ0=sQuery(id+"F0.wireOp",EDGE,"E2.right");var subQ1=sQuery(id+"F0.wireOp",EDGE,"E1.top");var subQ2=makeQuery(id+"F0.imprint","INTERSECT",VERTEX,{"derivedFrom":[subQ1,subQ0]});Q70=makeQuery(id+"F0.imprint","IMPRINT",FACE,{"disambiguationData":[TD([[makeQuery(id+"F0.imprint","IMPRINT",EDGE,{"disambiguationData":[TD([[subQ2,-1.0]])],"derivedFrom":subQ1}),-1.0]])]});}
            var Q71;
            {var subQ0=sQuery(id+"F0.wireOp",EDGE,"E5");var subQ1=sQuery(id+"F0.wireOp",EDGE,"E1.top");var subQ2=makeQuery(id+"F0.imprint","INTERSECT",VERTEX,{"disambiguationData":[OD(0.0)],"derivedFrom":[subQ1,subQ0]});Q71=makeQuery(id+"F0.imprint","IMPRINT",FACE,{"disambiguationData":[TD([[makeQuery(id+"F0.imprint","IMPRINT",EDGE,{"disambiguationData":[TD([[subQ2,-1.0]])],"derivedFrom":subQ1}),-1.0]])]});}
            var Q72;
            {var subQ0=sQuery(id+"F0.wireOp",EDGE,"E2.right");var subQ1=sQuery(id+"F0.wireOp",EDGE,"E1.bottom");var subQ2=makeQuery(id+"F0.imprint","INTERSECT",VERTEX,{"derivedFrom":[subQ1,subQ0]});Q72=makeQuery(id+"F0.imprint","IMPRINT",FACE,{"disambiguationData":[TD([[makeQuery(id+"F0.imprint","IMPRINT",EDGE,{"disambiguationData":[TD([[subQ2,-1.0]])],"derivedFrom":subQ1}),1.0]])]});}
            var Q73;
            {var subQ0=sQuery(id+"F0.wireOp",EDGE,"E5");var subQ1=sQuery(id+"F0.wireOp",EDGE,"E1.bottom");var subQ2=makeQuery(id+"F0.imprint","INTERSECT",VERTEX,{"disambiguationData":[OD(0.0)],"derivedFrom":[subQ1,subQ0]});Q73=makeQuery(id+"F0.imprint","IMPRINT",FACE,{"disambiguationData":[TD([[makeQuery(id+"F0.imprint","IMPRINT",EDGE,{"disambiguationData":[TD([[subQ2,-1.0]])],"derivedFrom":subQ1}),1.0]])]});}
            var Q74;
            {var subQ0=sQuery(id+"F0.wireOp",EDGE,"E4.left");Q74=makeQuery(id+"F0.imprint","IMPRINT",FACE,{"disambiguationData":[TD([[makeQuery(id+"F0.imprint","IMPRINT",EDGE,{"derivedFrom":subQ0}),1.0]])]});}
            var Q75;
            {var subQ0=sQuery(id+"F0.wireOp",EDGE,"E4.bottom");var subQ1=sQuery(id+"F0.wireOp",EDGE,"E2.left");var subQ2=makeQuery(id+"F0.imprint","INTERSECT",VERTEX,{"derivedFrom":[subQ1,subQ0]});Q75=makeQuery(id+"F0.imprint","IMPRINT",FACE,{"disambiguationData":[TD([[makeQuery(id+"F0.imprint","IMPRINT",EDGE,{"disambiguationData":[TD([[subQ2,-1.0]])],"derivedFrom":subQ1}),1.0]])]});}
            extrude(context, id + "F2", {"entities" : qUnion([Q0, Q1, Q2, Q3, Q4, Q5, Q6, Q7, Q8, Q9, Q10, Q11, Q12, Q13, Q14, Q15, Q16, Q17, Q18, Q19, Q20, Q21, Q22, Q23, Q24, Q25, Q26, Q27, Q28, Q29, Q30, Q31, Q32, Q33, Q34, Q35, Q36, Q37, Q38, Q39, Q40, Q41, Q42, Q43, Q44, Q45, Q46, Q47, Q48, Q49, Q50, Q51, Q52, Q53, Q54, Q55, Q56, Q57, Q58, Q59, Q60, Q61, Q62, Q63, Q64, Q65, Q66, Q67, Q68, Q69, Q70, Q71, Q72, Q73, Q74, Q75]), "operationType" : NewBodyOperationType.ADD, "depth" : 2 * mm});
        }
    });
